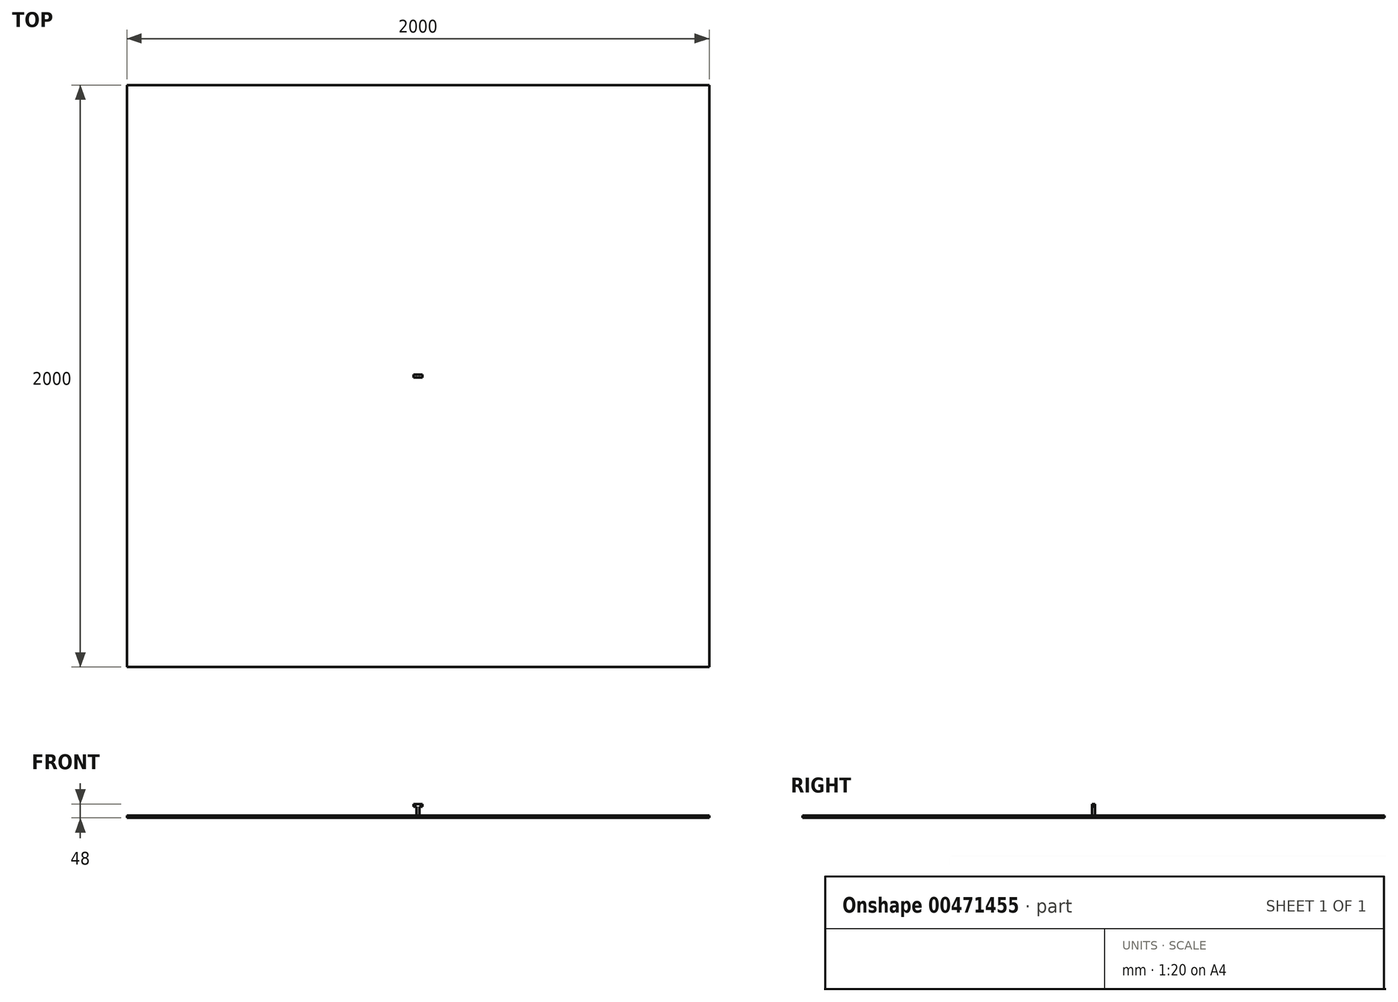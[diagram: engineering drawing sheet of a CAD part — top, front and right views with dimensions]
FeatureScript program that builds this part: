
annotation { "Feature Type Name" : "Feature", "Feature Type Description" : "" }
export const myFeature = defineFeature(function(context is Context, id is Id, definition is map)
    precondition{}
    {
        {
            var Q0;
            Q0=qCreatedBy(makeId("Front.planeOp"),FACE);
            var sketch = newSketch(context, id + "F0", { "sketchPlane" : qUnion([Q0])});
            skLineSegment(sketch, "E0", {"start": v(-15, 40) * mm, "end": v(15, 40) * mm});
            skLineSegment(sketch, "E1", {"start": v(15, 40) * mm, "end": v(15, 30) * mm});
            skLineSegment(sketch, "E2", {"start": v(15, 30) * mm, "end": v(5, 30) * mm});
            skLineSegment(sketch, "E3", {"start": v(5, 30) * mm, "end": v(5, 0) * mm});
            skLineSegment(sketch, "E4", {"start": v(5, 0) * mm, "end": v(-5, 0) * mm});
            skLineSegment(sketch, "E5.MirrorCS", {"start": v(-15, 40) * mm, "end": v(-15, 30) * mm});
            skLineSegment(sketch, "E6.MirrorCS", {"start": v(-15, 30) * mm, "end": v(-5, 30) * mm});
            skLineSegment(sketch, "E7.MirrorCS", {"start": v(-5, 30) * mm, "end": v(-5, 0) * mm});
            skSolve(sketch);
        }
        {
            var Q0;
            Q0=makeQuery(id+"F0.imprint","IMPRINT",FACE,{"disambiguationData":[TD([[makeQuery(id+"F0.imprint","IMPRINT",EDGE,{"derivedFrom":sQuery(id+"F0.wireOp",EDGE,"E0")}),-1.0]])]});
            extrude(context, id + "F1", {"entities" : qUnion([Q0]), "endBound" : BoundingType.SYMMETRIC, "depth" : 10 * mm});
        }
        {
            var Q0;
            Q0=qCreatedBy(makeId("Top.planeOp"),FACE);
            var sketch = newSketch(context, id + "F2", { "sketchPlane" : qUnion([Q0])});
            skLineSegment(sketch, "E8.bottom", {"start": v(-1000, 1000) * mm, "end": v(1000, 1000) * mm});
            skLineSegment(sketch, "E8.top", {"start": v(-1000, -1000) * mm, "end": v(1000, -1000) * mm});
            skLineSegment(sketch, "E8.left", {"start": v(-1000, 1000) * mm, "end": v(-1000, -1000) * mm});
            skLineSegment(sketch, "E8.right", {"start": v(1000, 1000) * mm, "end": v(1000, -1000) * mm});
            skSolve(sketch);
        }
        {
            var Q0;
            Q0=makeQuery(id+"F2.imprint","IMPRINT",FACE,{"disambiguationData":[TD([[makeQuery(id+"F2.imprint","IMPRINT",EDGE,{"derivedFrom":sQuery(id+"F2.wireOp",EDGE,"E8.bottom")}),-1.0]])]});
            extrude(context, id + "F3", {"entities" : qUnion([Q0]), "oppositeDirection" : true, "depth" : 8 * mm});
        }
    });
